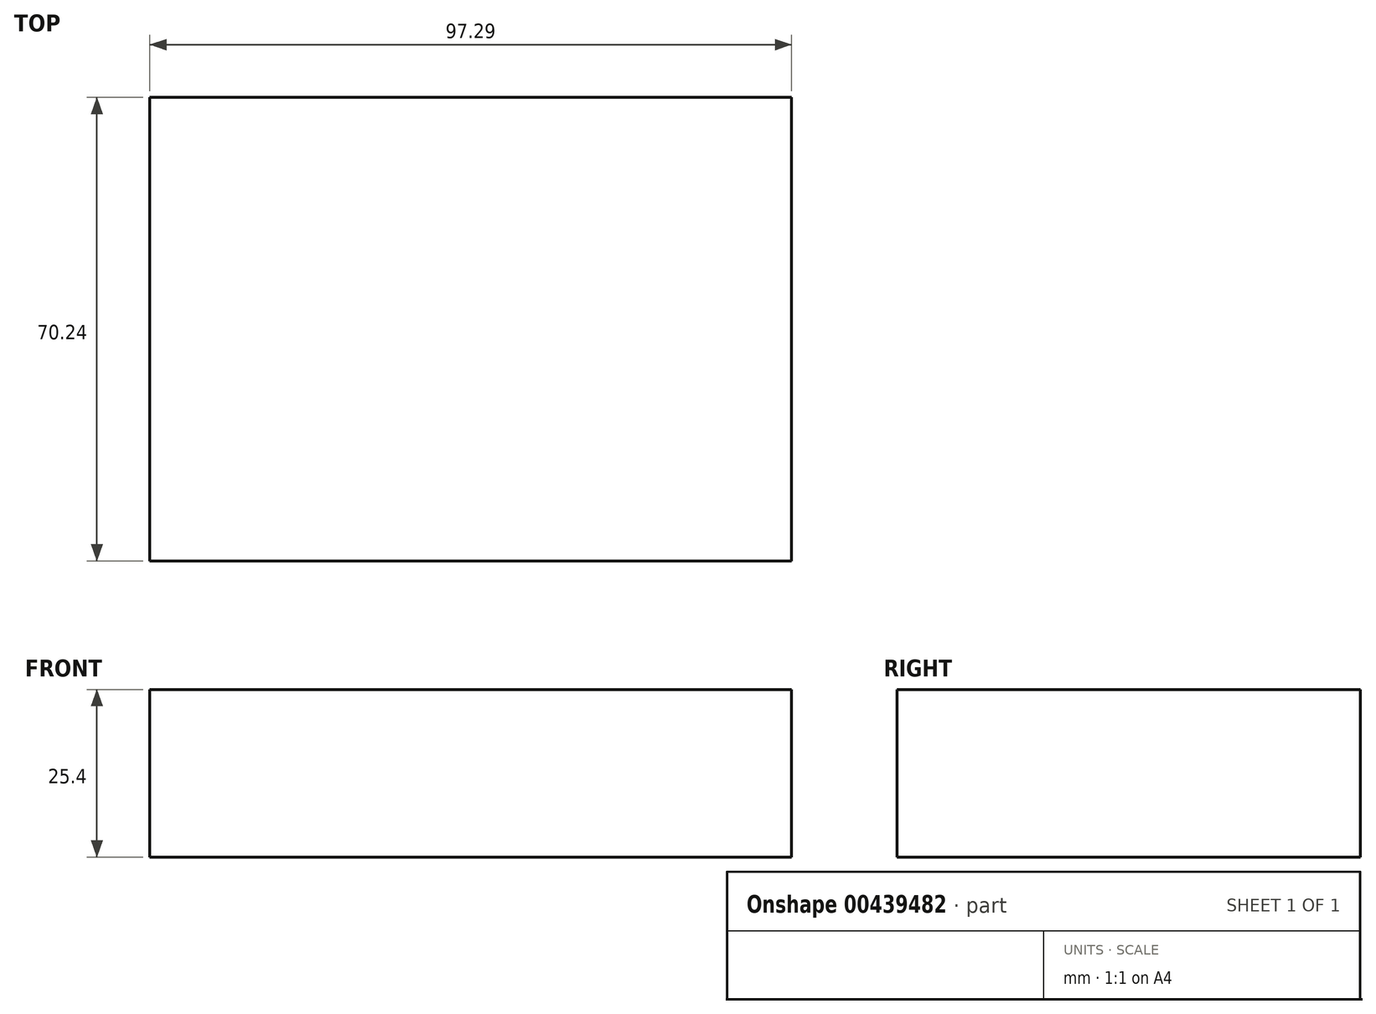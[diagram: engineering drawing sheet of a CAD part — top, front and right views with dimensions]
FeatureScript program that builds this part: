
annotation { "Feature Type Name" : "Feature", "Feature Type Description" : "" }
export const myFeature = defineFeature(function(context is Context, id is Id, definition is map)
    precondition{}
    {
        {
            var Q0;
            Q0=qCreatedBy(makeId("Top.planeOp"),FACE);
            var sketch = newSketch(context, id + "F0", { "sketchPlane" : qUnion([Q0])});
            skLineSegment(sketch, "E0.bottom", {"start": v(-51.03, 35.69) * mm, "end": v(46.26, 35.69) * mm});
            skLineSegment(sketch, "E0.top", {"start": v(-51.03, -34.55) * mm, "end": v(46.26, -34.55) * mm});
            skLineSegment(sketch, "E0.left", {"start": v(-51.03, 35.69) * mm, "end": v(-51.03, -34.55) * mm});
            skLineSegment(sketch, "E0.right", {"start": v(46.26, 35.69) * mm, "end": v(46.26, -34.55) * mm});
            skSolve(sketch);
        }
        {
            var Q0;
            Q0=makeQuery(id+"F0.imprint","IMPRINT",FACE,{"disambiguationData":[TD([[makeQuery(id+"F0.imprint","IMPRINT",EDGE,{"derivedFrom":sQuery(id+"F0.wireOp",EDGE,"E0.bottom")}),-1.0]])]});
            extrude(context, id + "F1", {"entities" : qUnion([Q0]), "depth" : 25.4 * mm});
        }
    });
